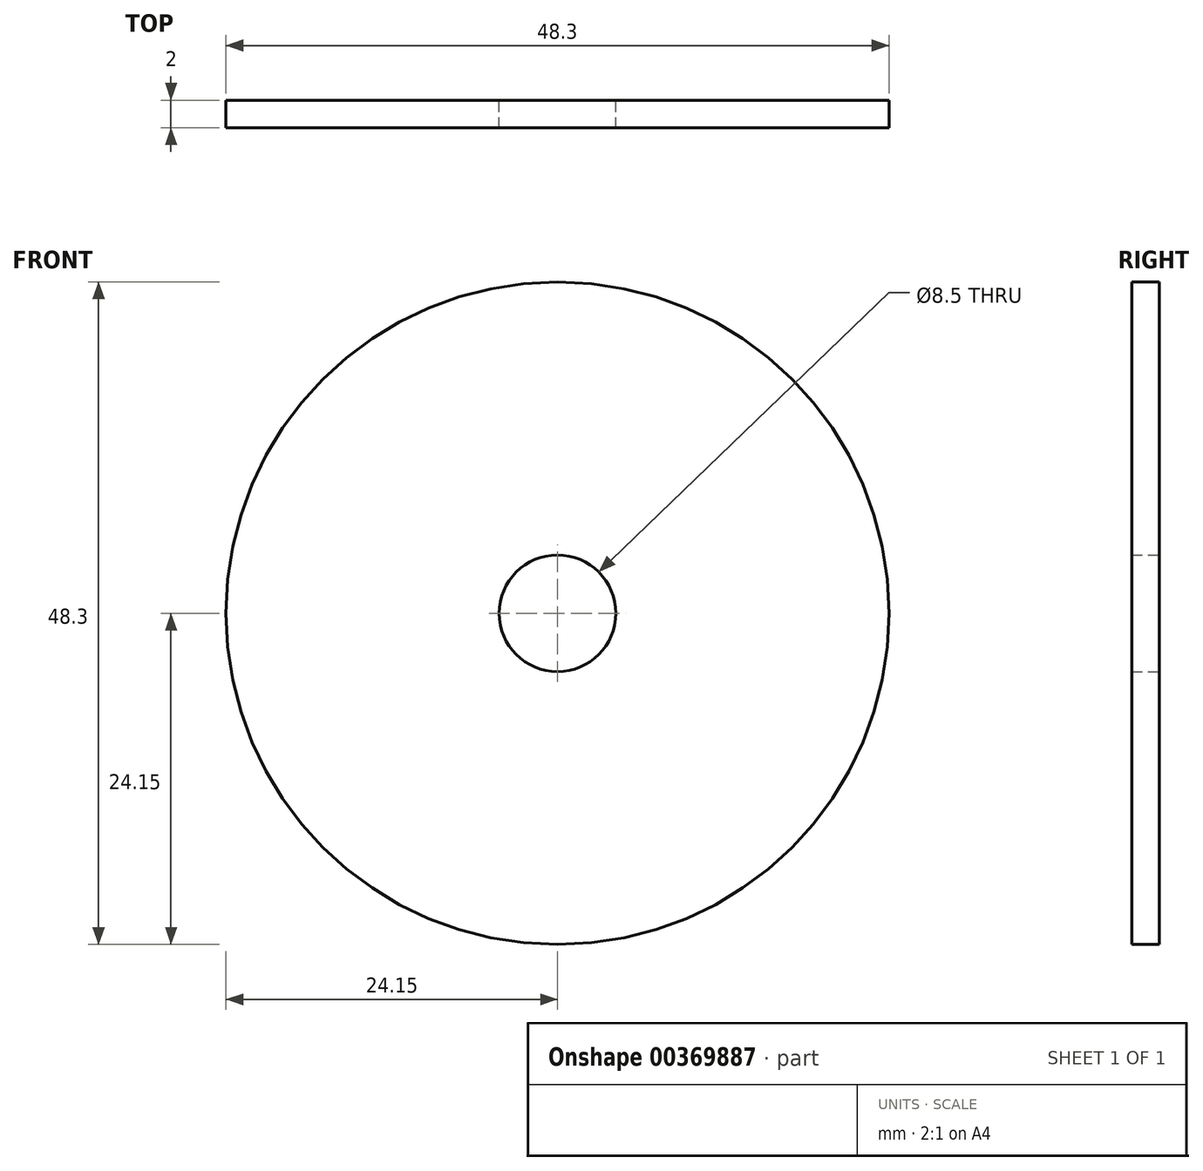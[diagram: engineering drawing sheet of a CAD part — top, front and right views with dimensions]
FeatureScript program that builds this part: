
annotation { "Feature Type Name" : "Feature", "Feature Type Description" : "" }
export const myFeature = defineFeature(function(context is Context, id is Id, definition is map)
    precondition{}
    {
        {
            var Q0;
            Q0=qCreatedBy(makeId("Front.planeOp"),FACE);
            var sketch = newSketch(context, id + "F0", { "sketchPlane" : qUnion([Q0])});
            skCircle(sketch, "E0", {"center": v(0, 0) * mm, "radius": 24.15 * mm});
            skSolve(sketch);
        }
        {
            var Q0;
            Q0=makeQuery(id+"F0.imprint","IMPRINT",FACE,{"disambiguationData":[TD([[makeQuery(id+"F0.imprint","IMPRINT",EDGE,{"derivedFrom":sQuery(id+"F0.wireOp",EDGE,"E0")}),1.0]])]});
            extrude(context, id + "F1", {"entities" : qUnion([Q0]), "depth" : 2 * mm});
        }
        {
            var Q0;
            Q0=sQuery(id+"F0.wireOp",VERTEX,"E0.center");
            var Q1;
            Q1=makeQuery(id+"F1.opExtrude","SWEPT_BODY",BODY,{"disambiguationData":[OSD([sQuery(id+"F0.wireOp",EDGE,"E0")])]});
            hole(context, id + "F2", {"style" : HoleStyle.SIMPLE, "endStyle" : HoleEndStyle.THROUGH, "oppositeDirection" : true, "holeDiameter" : 8.5 * mm, "isTappedThrough" : true, "tappedDepth" : 12 * mm, "tapClearance" : 3, "locations" : qUnion([Q0]), "scope" : qUnion([Q1])});
        }
    });
